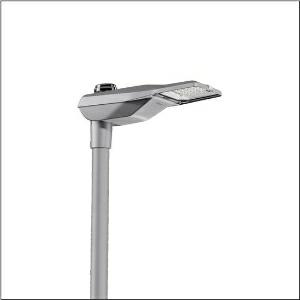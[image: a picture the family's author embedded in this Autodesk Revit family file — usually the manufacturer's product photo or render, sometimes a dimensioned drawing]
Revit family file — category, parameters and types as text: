
# Revit family: streetlight_sl_21_micro___stw1_0a_5xe5e37n08db_8c5c
name_source: partatom
category: Lighting Fixtures
units: mm (PartAtom-declared; Revit-internal decimal feet)

## family parameters
Cut with Voids When Loaded = No
Host = Face
Light Source = No
Part Type = Normal
Room Calculation Point = No
Round Connector Dimension = Use Diameter
Shared = No

## types (1)
- --- (1 x LED, 5110 lm, 39.1 W, 3000K)
    Apparent Load = 39 VA
    CIE Flux Codes = 38 75 98 100 100
    Color Rendering = 70
    Color Temperature = 3000K
    Default Elevation = 1800 mm
    Description = Streetlight SL 21 micro, mast luminaire, primary light control with lens, of PMMA, primary optical cover: cover, of toughened safety glass, transparent, light distribution: STW1.0a, light emission: direct distribution, primary light characteristic: asymmetric, installation type: post-top, LED, 3G 1.5mm², High Power LED, rated luminous flux: 5.110lm, luminous efficacy: 131lm/W, light colour: 730, colour temperature: 3000K, control gear: NEMA (7pin), control: overheat protection, pre-setting: linear dimming characteristic, constant luminous flux control, time-dependent luminous flux control, flexible luminous flux parameterisation, mains connection: 230..240V, AC, 50/60Hz, connection cable pre-assembled, cable length: 6,5m, wiring characteristics: H07RN-F, start of lifetime: 39W, end of service life: 41W, reduction: 18W, luminaire housing, of diecast aluminium (EN AC-44300), powder-coated, Siteco® metallic grey (DB 702S), corrosivity category C5 mid according to DIN EN ISO 12944, multi-level sealing system, sealing non-destructively replaceable, inclination adjustable: 0°, 5°, 10°, 15°, length: 528mm, width: 235mm, height: 110mm, spigot size: 76/60mm (post-top), mounting height: 4..8m, protection rating (complete): IP66, insulation class (complete): insulation class I (protective earthing), certification: CE, ENEC, ENEC+, VDE, impact resistance: IK10, permissible operating ambient temperature for outdoor applications: -40..+50°C, standard-compliant lighting for roads and squares, packaging unit: 1 piece

Light Distribution: STW1.0a
    Height = 110 mm
    Lamp = 1 x LED
    Lamp Light Flux = 5110 lm
    Lamp Power = 39.1 W
    Lamp count = 1
    Length = 528 mm
    Luminous efficacy = 131 lm/W
    Manufacturer = Siteco
    ModVariant = No
    Model = 5XE5E37N08DB
    Number of Poles = 1
    OnlyDefault = Yes
    Power Factor = 1
    Product Name = Streetlight SL 21 micro | STW1.0a
    Product group = mast luminaire | pylon top
    ProductGroupID = 6100
    Protection Class = Protection class I
    Protection Degree = IP 66
    RLX_Detail_Level = 1
    RLX_Emergency_Light_Flux = 0 lm
    RLX_Emergency_Type = 0
    RLX_Emergency_Type_DB = No
    RlxData = <blob elided: 98901 chars, md5=bc56af2d>
    Socket = socket
    Standby Power = 0 W
    System Light Flux = 5110 lm
    System Power = 39 W
    Type Comments = factory setting: luminous flux: 100 % | dim-lin: 254 | 765 mA
    Type Image = l_1294375.jpg
    URL = http://relux.com
    VarID = @adj_157303
    Voltage = 0 V
    Weight = 0.00 kg
    Width = 235 mm

## geometry (parser evidence)
native form markers: Blend x4, Sweep x10
no freeform markers — native parametric forms only
